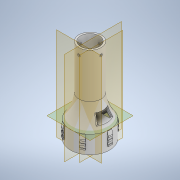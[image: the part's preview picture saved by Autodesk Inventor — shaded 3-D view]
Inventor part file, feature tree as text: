
AUTODESK INVENTOR PART (.ipt)
format: ipt  version: 2022.3 (Build 263350000, 350)  size: 583,680 bytes
history: native  units: mm
features: revolve x12, sketch x8, extrude x6, plane x4, hole x3, pattern_circular x2, mirror x2
ambient origin geometry x8: Origin, YZ Plane, XZ Plane, XY Plane, X Axis, Y Axis, Z Axis, Center Point
bodies: Solid1 (feature_tree)
feature tree (37):
  extrude  "Extrusion1"  Depth=4.0mm
  sketch  "Sketch2"  dims[d2=40.0mm d3=0.0mm d4=88.0mm]
  revolve  "Revolution1"  [1 undecoded]
  plane  "Work Plane1"
  extrude  "Extrusion2"  Depth=100.0mm
  sketch  "Sketch18"  dims[d5=50.0mm d8=100.0mm]
  extrude  "Extrusion11"  Depth=100.0mm
  extrude  "Extrusion12"  Depth=100.0mm
  extrude  "Extrusion13"  [1 undecoded]
  pattern_circular  "Circular Pattern2"  [2 undecoded]
  revolve  "Revolution4"  [1 undecoded]
  plane  "Work Plane3"
  plane  "Work Plane4"
  hole  "Hole5"  [1 undecoded]
  hole  "Hole6"  [1 undecoded]
  mirror  "Mirror1"
  mirror  "Mirror2"
  extrude  "Extrusion15"  Depth=5.0mm TaperAngle=0.0deg
  plane  "Work Plane5"
  sketch  "Sketch24"  dims[d16=75.0mm d17=75.0mm d18=5.0mm d19=15.0mm d20=5.2mm d21=5.0mm d22=0.0mm d79=0.0mm d106=4.0mm d107=10.0mm d108=30.0mm d109=0.0mm d110=10.0mm d111=30.0mm d112=0.0mm d113=1.0mm d114=10.0mm d115=1.0mm d116=3.0mm d117=1.0mm d118=5.0mm d119=1.0mm d120=4.0mm d121=1.0mm d122=5.0mm d123=10.0mm d124=90.0deg d131=10.0mm d132=0.0mm d133=1.0mm d134=3.0mm d135=60.0mm d136=360.0deg d138=2.0mm d139=5.0mm d140=2.0mm d141=5.0mm d142=90.0deg d143=25.0mm d144=25.0mm d145=30.0mm d146=3.4mm d147=6.0mm d148=5.9mm d149=2.0mm d150=90.0deg d151=4.2mm d152=0.0mm d153=30.0mm d154=180.0deg d155=3.4mm d156=6.0mm d157=5.9mm d158=2.0mm d159=90.0deg d160=4.2mm d161=0.0mm d165=4.0mm d166=10.0mm d167=0.0mm d168=6.6mm d179=210.0deg d180=150.0deg d181=10.0mm d182=10.0mm d183=90.0deg d184=5.0mm d185=2.0mm d186=2.2mm d187=6.0mm d188=3.1mm d189=4.1mm d190=90.0deg d191=0.9mm d192=0.0mm d193=20.0mm d194=90.0deg d196=20.0mm d197=20.0mm d198=15.0mm d199=10.0mm d200=120.0deg d201=60.0deg d202=10.0mm d203=10.0mm d204=10.0mm d205=1.0mm d206=5.0mm d207=2.0mm d208=5.0mm d209=1.0mm d210=210.0deg d211=35.77925mm d212=27.052603mm d213=20.071286mm d214=11.34464mm d125=0.872665mm d126=0.872665mm d137=14.3117mm d164=2.25mm]
  revolve  "Revolution5"  [1 undecoded]
  revolve  "Revolution6"  [1 undecoded]
  revolve  "Revolution7"  [1 undecoded]
  hole  "Hole8"  [1 undecoded]
  pattern_circular  "Circular Pattern4"  [2 undecoded]
  revolve  "Revolution8"  [1 undecoded]
  revolve  "Revolution9"  [1 undecoded]
  revolve  "Revolution10"  [1 undecoded]
  revolve  "Revolution11"  [1 undecoded]
  revolve  "Revolution12"  [1 undecoded]
  revolve  "Revolution13"  [1 undecoded]
  revolve  "Revolution14"  [1 undecoded]
  sketch  "Sketch1"  dims[d0=80.0mm d1=4.0mm]
  sketch  "Sketch19"  dims[d9=25.0mm d10=100.0mm]
  sketch  "Sketch20"  dims[d11=4.0mm d12=100.0mm]
  sketch  "Sketch21"  dims[d13=360.0deg d14=-45.0mm]
  sketch  "Sketch22"  dims[d15=5.0mm]
note: 20 required parameter values undecoded (feature->parameter linkage not recoverable at this tier; creation-order binding heuristic only, values carry confidence <= 0.55)